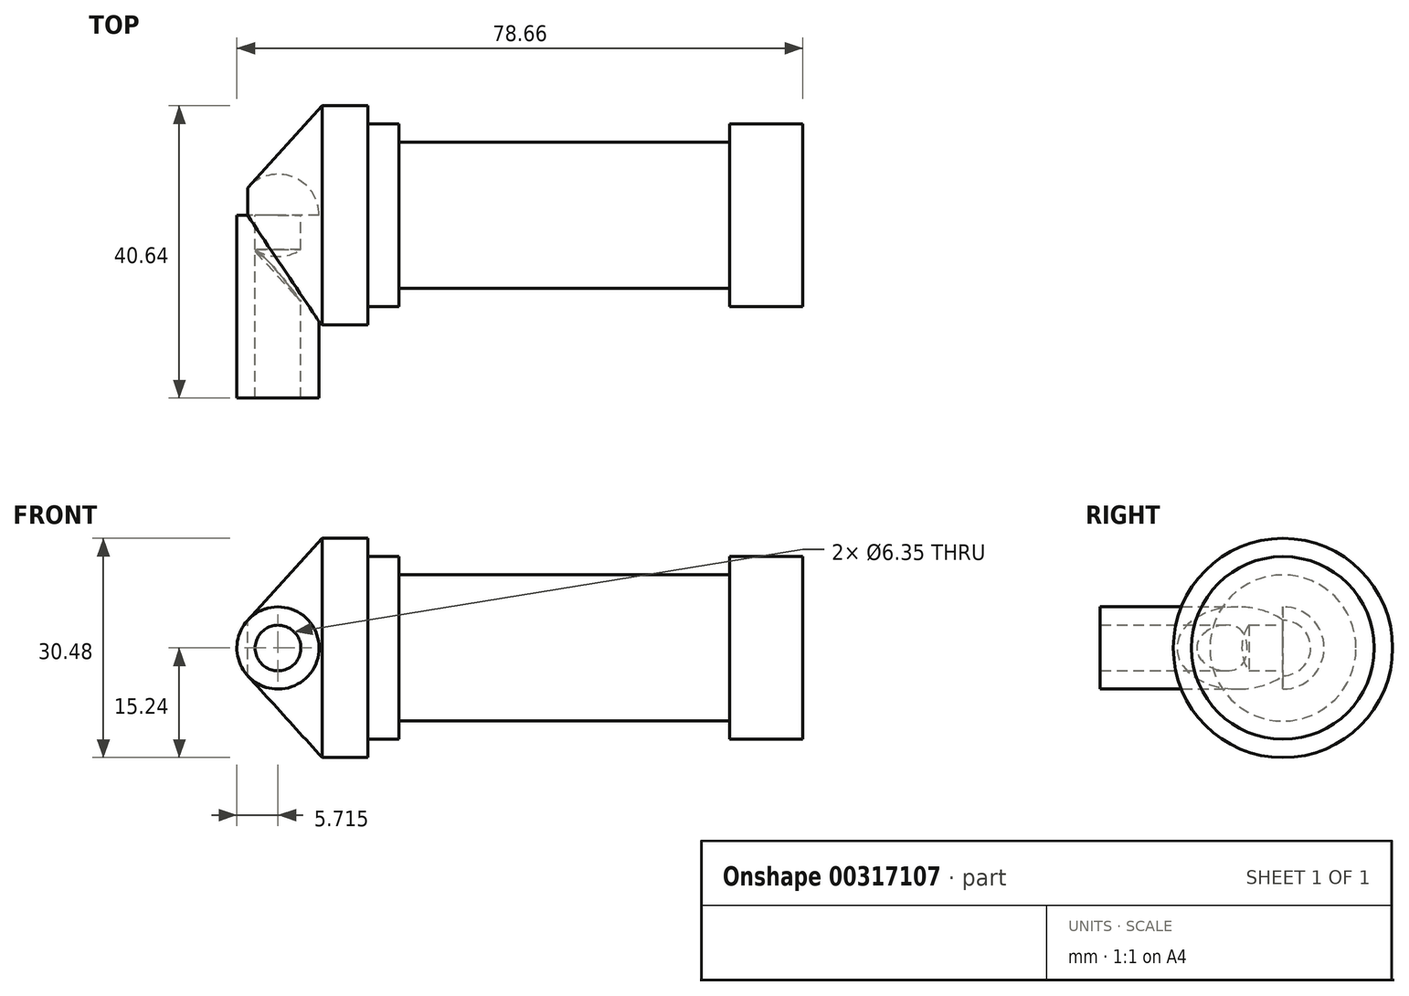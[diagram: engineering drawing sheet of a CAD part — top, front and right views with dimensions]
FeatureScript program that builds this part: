
annotation { "Feature Type Name" : "Feature", "Feature Type Description" : "" }
export const myFeature = defineFeature(function(context is Context, id is Id, definition is map)
    precondition{}
    {
        {
            var Q0;
            Q0=qCreatedBy(makeId("Front.planeOp"),FACE);
            var sketch = newSketch(context, id + "F0", { "sketchPlane" : qUnion([Q0])});
            skLineSegment(sketch, "E0", {"start": v(0, 0) * mm, "end": v(0, 12.7) * mm});
            skLineSegment(sketch, "E1", {"start": v(0, 12.7) * mm, "end": v(10.16, 12.7) * mm});
            skLineSegment(sketch, "E2", {"start": v(10.16, 12.7) * mm, "end": v(10.16, 10.16) * mm});
            skLineSegment(sketch, "E3", {"start": v(10.16, 10.16) * mm, "end": v(56.13, 10.16) * mm});
            skLineSegment(sketch, "E4", {"start": v(56.13, 10.16) * mm, "end": v(56.13, 12.7) * mm});
            skLineSegment(sketch, "E5", {"start": v(56.13, 12.7) * mm, "end": v(66.3, 12.7) * mm});
            skLineSegment(sketch, "E6", {"start": v(66.3, 12.7) * mm, "end": v(66.3, 0) * mm});
            skLineSegment(sketch, "E7", {"start": v(66.3, 0) * mm, "end": v(0, 0) * mm});
            skLineSegment(sketch, "E8", {"start": v(5.84, 15.24) * mm, "end": v(-0.5, 15.24) * mm});
            skLineSegment(sketch, "E9", {"start": v(-0.5, 15.24) * mm, "end": v(-10.88, 3.85) * mm});
            skLineSegment(sketch, "E10", {"start": v(0, 0) * mm, "end": v(-6.65, 0) * mm});
            skCircle(sketch, "E11", {"center": v(-6.65, 0) * mm, "radius": 5.72 * mm});
            skCircle(sketch, "E12", {"center": v(-6.65, 0) * mm, "radius": 3.18 * mm});
            skLineSegment(sketch, "E13", {"start": v(5.84, 15.24) * mm, "end": v(5.84, -9.4) * mm});
            skLineSegment(sketch, "E14", {"start": v(5.84, -9.4) * mm, "end": v(-8.18, -5.5) * mm});
            skSolve(sketch);
        }
        {
            var Q0;
            {var subQ0=sQuery(id+"F0.wireOp",EDGE,"E0");Q0=makeQuery(id+"F0.imprint","IMPRINT",FACE,{"disambiguationData":[TD([[makeQuery(id+"F0.imprint","IMPRINT",EDGE,{"derivedFrom":subQ0}),-1.0]])]});}
            var Q1;
            {var subQ1=sQuery(id+"F0.wireOp",EDGE,"E0");Q1=makeQuery(id+"F0.imprint","IMPRINT",FACE,{"disambiguationData":[TD([[makeQuery(id+"F0.imprint","IMPRINT",EDGE,{"derivedFrom":subQ1}),1.0]])]});}
            var Q2;
            Q2=sQuery(id+"F0.wireOp",EDGE,"E7");
            revolve(context, id + "F1", {"entities" : qUnion([Q0, Q1]), "axis" : qUnion([Q2]), "revolveType" : RevolveType.FULL});
        }
        {
            var Q0;
            {var subQ0=sQuery(id+"F0.wireOp",EDGE,"E2");Q0=makeQuery(id+"F0.imprint","IMPRINT",FACE,{"disambiguationData":[TD([[makeQuery(id+"F0.imprint","IMPRINT",EDGE,{"derivedFrom":subQ0}),-1.0]])]});}
            var Q1;
            Q1=sQuery(id+"F0.wireOp",EDGE,"E7");
            revolve(context, id + "F2", {"operationType" : NewBodyOperationType.ADD, "entities" : qUnion([Q0]), "axis" : qUnion([Q1]), "revolveType" : RevolveType.FULL});
        }
        {
            var Q0;
            {var subQ5=sQuery(id+"F0.wireOp",EDGE,"E12");Q0=makeQuery(id+"F0.imprint","IMPRINT",FACE,{"disambiguationData":[TD([[makeQuery(id+"F0.imprint","IMPRINT",EDGE,{"derivedFrom":subQ5}),-1.0]])]});}
            extrude(context, id + "F3", {"entities" : qUnion([Q0]), "operationType" : NewBodyOperationType.ADD, "depth" : 25.4 * mm});
        }
    });
